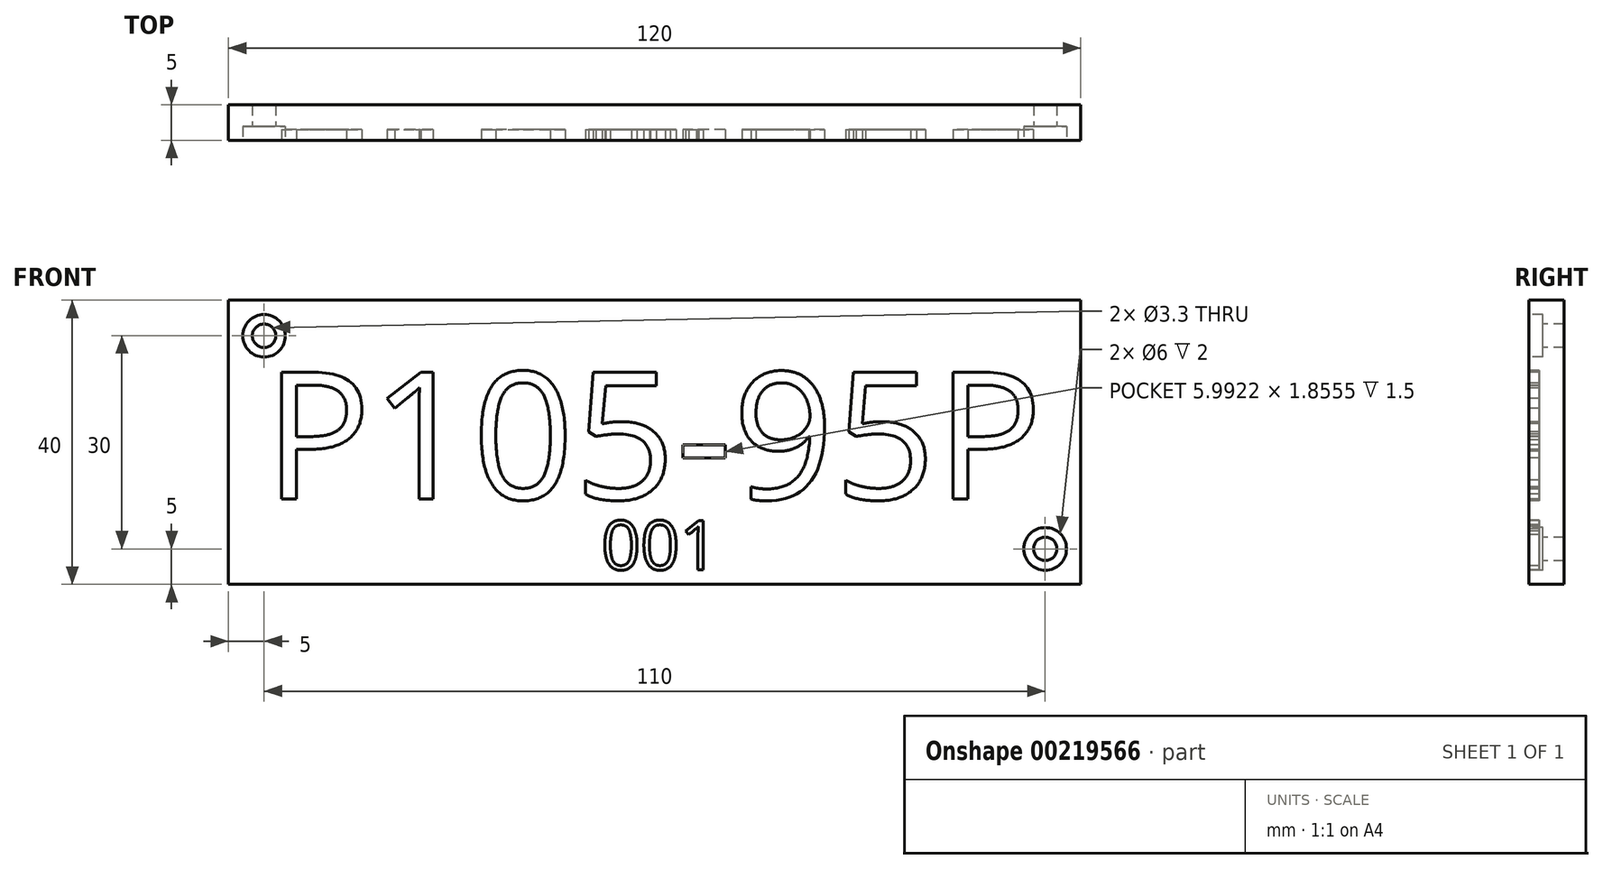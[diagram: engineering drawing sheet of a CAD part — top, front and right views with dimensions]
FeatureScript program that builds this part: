
annotation { "Feature Type Name" : "Feature", "Feature Type Description" : "" }
export const myFeature = defineFeature(function(context is Context, id is Id, definition is map)
    precondition{}
    {
        {
            var Q0;
            Q0=qCreatedBy(makeId("Front.planeOp"),FACE);
            var sketch = newSketch(context, id + "F0", { "sketchPlane" : qUnion([Q0])});
            skLineSegment(sketch, "E0.bottom", {"start": v(60, -20) * mm, "end": v(-60, -20) * mm});
            skLineSegment(sketch, "E0.top", {"start": v(60, 20) * mm, "end": v(-60, 20) * mm});
            skLineSegment(sketch, "E0.left", {"start": v(60, -20) * mm, "end": v(60, 20) * mm});
            skLineSegment(sketch, "E0.right", {"start": v(-60, -20) * mm, "end": v(-60, 20) * mm});
            skPoint(sketch, "E0.middle", {"position": v(0, 0) * mm});
            skSolve(sketch);
        }
        {
            var Q0;
            Q0=makeQuery(id+"F0.imprint","IMPRINT",FACE,{"disambiguationData":[TD([[makeQuery(id+"F0.imprint","IMPRINT",EDGE,{"derivedFrom":sQuery(id+"F0.wireOp",EDGE,"E0.bottom")}),-1.0]])]});
            extrude(context, id + "F1", {"entities" : qUnion([Q0]), "depth" : 5 * mm});
        }
        {
            var Q0;
            Q0=makeQuery(id+"F1.opExtrude","CAP_FACE",FACE,{"disambiguationData":[OSD([sQuery(id+"F0.wireOp",EDGE,"E0.bottom"),sQuery(id+"F0.wireOp",EDGE,"E0.top"),sQuery(id+"F0.wireOp",EDGE,"E0.left"),sQuery(id+"F0.wireOp",EDGE,"E0.right")])],"isStart":false});
            var sketch = newSketch(context, id + "F2", { "sketchPlane" : qUnion([Q0])});
            skLineSegment(sketch, "E1", {"start": v(-60, 15) * mm, "end": v(60, 15) * mm});
            skPoint(sketch, "E2", {"position": v(-55, 15) * mm});
            skSolve(sketch);
        }
        {
            var Q0;
            Q0=sQuery(id+"F2.wireOp",VERTEX,"E2");
            var Q1;
            Q1=makeQuery(id+"F1.opExtrude","SWEPT_BODY",BODY,{"disambiguationData":[OSD([sQuery(id+"F0.wireOp",EDGE,"E0.bottom"),sQuery(id+"F0.wireOp",EDGE,"E0.top"),sQuery(id+"F0.wireOp",EDGE,"E0.left"),sQuery(id+"F0.wireOp",EDGE,"E0.right")])]});
            hole(context, id + "F3", {"style" : HoleStyle.C_BORE, "endStyle" : HoleEndStyle.THROUGH, "holeDiameter" : 3.3 * mm, "cBoreDiameter" : 6 * mm, "cBoreDepth" : 2 * mm, "locations" : qUnion([Q0]), "scope" : qUnion([Q1]), "isTappedThrough" : true});
        }
        {
            var Q0;
            Q0=makeQuery(id+"F1.opExtrude","CAP_FACE",FACE,{"disambiguationData":[OSD([sQuery(id+"F0.wireOp",EDGE,"E0.bottom"),sQuery(id+"F0.wireOp",EDGE,"E0.top"),sQuery(id+"F0.wireOp",EDGE,"E0.left"),sQuery(id+"F0.wireOp",EDGE,"E0.right")])],"isStart":false});
            var sketch = newSketch(context, id + "F4", { "sketchPlane" : qUnion([Q0])});
            skLineSegment(sketch, "E3", {"start": v(-60, -15) * mm, "end": v(60, -15) * mm});
            skPoint(sketch, "E4", {"position": v(55, -15) * mm});
            skSolve(sketch);
        }
        {
            var Q0;
            Q0=sQuery(id+"F4.wireOp",VERTEX,"E4");
            var Q1;
            Q1=makeQuery(id+"F1.opExtrude","SWEPT_BODY",BODY,{"disambiguationData":[OSD([sQuery(id+"F0.wireOp",EDGE,"E0.bottom"),sQuery(id+"F0.wireOp",EDGE,"E0.top"),sQuery(id+"F0.wireOp",EDGE,"E0.left"),sQuery(id+"F0.wireOp",EDGE,"E0.right")])]});
            hole(context, id + "F5", {"style" : HoleStyle.C_BORE, "endStyle" : HoleEndStyle.THROUGH, "holeDiameter" : 3.3 * mm, "cBoreDiameter" : 6 * mm, "cBoreDepth" : 2 * mm, "locations" : qUnion([Q0]), "scope" : qUnion([Q1]), "isTappedThrough" : true});
        }
        {
            var Q0;
            Q0=makeQuery(id+"F1.opExtrude","CAP_FACE",FACE,{"disambiguationData":[OSD([sQuery(id+"F0.wireOp",EDGE,"E0.bottom"),sQuery(id+"F0.wireOp",EDGE,"E0.top"),sQuery(id+"F0.wireOp",EDGE,"E0.left"),sQuery(id+"F0.wireOp",EDGE,"E0.right")])],"isStart":false});
            var sketch = newSketch(context, id + "F6", { "sketchPlane" : qUnion([Q0])});
            skText(sketch, "E5", { "text": "P105-95P", "fontName": "OpenSans-Regular.ttf"});
            const initialGuessF6  = {"E5": [-0.055, -0.008, 1, 0, 0.018]};
            skSetInitialGuess(sketch, initialGuessF6);
            skSolve(sketch);
        }
        {
            var Q0;
            Q0 = qSketchRegion(id + "F6", true);
            extrude(context, id + "F7", {"entities" : qUnion([Q0]), "operationType" : NewBodyOperationType.REMOVE, "oppositeDirection" : true, "depth" : 1.5 * mm});
        }
        {
            var Q0;
            {var subQ0=sQuery(id+"F0.wireOp",EDGE,"E0.bottom");var subQ1=sQuery(id+"F0.wireOp",EDGE,"E0.top");var subQ2=sQuery(id+"F0.wireOp",EDGE,"E0.left");var subQ3=sQuery(id+"F0.wireOp",EDGE,"E0.right");Q0=makeQuery(id+"F7.boolean.opBoolean","SPLIT",FACE,{"disambiguationData":[TD([makeQuery(id+"F1.opExtrude","SWEPT_FACE",FACE,{"disambiguationData":[OSD([subQ0])]})])],"derivedFrom":makeQuery(id+"F1.opExtrude","CAP_FACE",FACE,{"disambiguationData":[OSD([subQ0,subQ1,subQ2,subQ3])],"isStart":false})});}
            var sketch = newSketch(context, id + "F8", { "sketchPlane" : qUnion([Q0])});
            skText(sketch, "E6", { "text": "001", "fontName": "OpenSans-Regular.ttf"});
            const initialGuessF8  = {"E6": [-0.0075, -0.01793, 1, 0, 0.00693]};
            skSetInitialGuess(sketch, initialGuessF8);
            skSolve(sketch);
        }
        {
            var Q0;
            Q0 = qSketchRegion(id + "F8", true);
            extrude(context, id + "F9", {"entities" : qUnion([Q0]), "operationType" : NewBodyOperationType.REMOVE, "oppositeDirection" : true, "depth" : 1.5 * mm});
        }
    });
